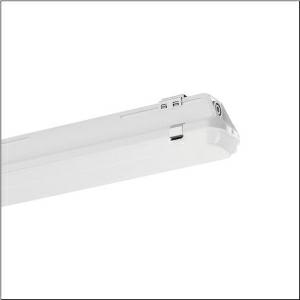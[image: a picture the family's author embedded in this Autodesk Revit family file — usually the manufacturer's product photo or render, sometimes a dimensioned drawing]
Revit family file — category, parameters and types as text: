
# Revit family: monsun_r__21_51fb10dl420k_c4f4
name_source: partatom
category: Lighting Fixtures
units: mm (PartAtom-declared; Revit-internal decimal feet)

## family parameters
Cut with Voids When Loaded = No
Host = Face
Light Source = No
Part Type = Normal
Room Calculation Point = No
Round Connector Dimension = Use Diameter
Shared = No

## types (1)
- --- (1 x LED, 2630 lm, 15.4 W, 4000K)
    Apparent Load = 15 VA
    CIE Flux Codes = 46 76 93 94 100
    Color Rendering = 80
    Color Temperature = 4000K
    Default Elevation = 1800 mm
    Description = Monsun® 21, damp-proof luminaire, chain hanger, primary optical cover: enclosure, of PMMA, light emission: direct distribution, primary light characteristic: symmetric, installation type: suspended mounting, surface-mounted, horizontal mounting, vertical mounting, LED, rated luminous flux: 2.630lm, luminous efficacy: 171lm/W, light colour: 840, colour temperature: 4000K, control gear: DALI 2, with terminal, 5-pole, max. 2.5mm², mains connection: 220..240V, AC, 50/60Hz, rated input power: 15W, housing, of glass-fibre reinforced plastic, uncoated, bright grey, incl. chain hanger, length: 1.299mm, width: 90mm, height: 88mm, clip for enclosure, of stainless steel (V2A), ceiling mounting element, of stainless steel (V2A), chain hanger, of stainless steel (V2A), protection rating (complete): IP66, insulation class (complete): insulation class I (protective earthing), certification: CE, ENEC, VDE, UKCA, protection symbol: D, impact resistance: IK04, permissible operating ambient temperature: -25..+35°C, standard: EN 50419, EN 60598-2-1, corresponds to IFS (International Featured Standards) requirements for safety and quality in the food industry, for indoor or canopied outdoor use, no direct snow, no direct sun, no direct rain, LABS conformity tested according to VDMA 24364:2018-05, contact your sales advisor before using the luminaires in applications with unclear chemical exposure, large temperature fluctuations or condensation-forming humidity, packaging unit: 1 piece
    Height = 88 mm
    Lamp = 1 x LED
    Lamp Light Flux = 2630 lm
    Lamp Power = 15.4 W
    Lamp count = 1
    Length = 1299 mm
    Luminous efficacy = 171 lm/W
    Manufacturer = Siteco
    ModVariant = No
    Model = 51FB10DL420K
    Mounting Place = Ceiling
    Mounting Type = Surface mounted
    Number of Poles = 1
    OnlyDefault = Yes
    Power Factor = 1
    Product Name = Monsun® 21
    Product group = damp-proof luminaire
    ProductGroupID = 300
    Protection Class = Protection class I
    Protection Degree = IP 66
    RLX_Detail_Level = 1
    RLX_Emergency_Light_Flux = 0 lm
    RLX_Emergency_Type = 0
    RLX_Emergency_Type_DB = No
    RlxData = <blob elided: 93333 chars, md5=55ca2120>
    Socket = socket
    Standby Power = 0 W
    System Light Flux = 2630 lm
    System Power = 15 W
    Type Comments = factory setting: luminous flux: 100 % | dim-lin: 254 | 98 mA
    Type Image = l_1319656.jpg
    URL = http://relux.com
    VarID = @adj_022534
    Voltage = 0 V
    Weight = 0.00 kg
    Width = 90 mm

## geometry (parser evidence)
native form markers: Blend x4, Sweep x12
no freeform markers — native parametric forms only
